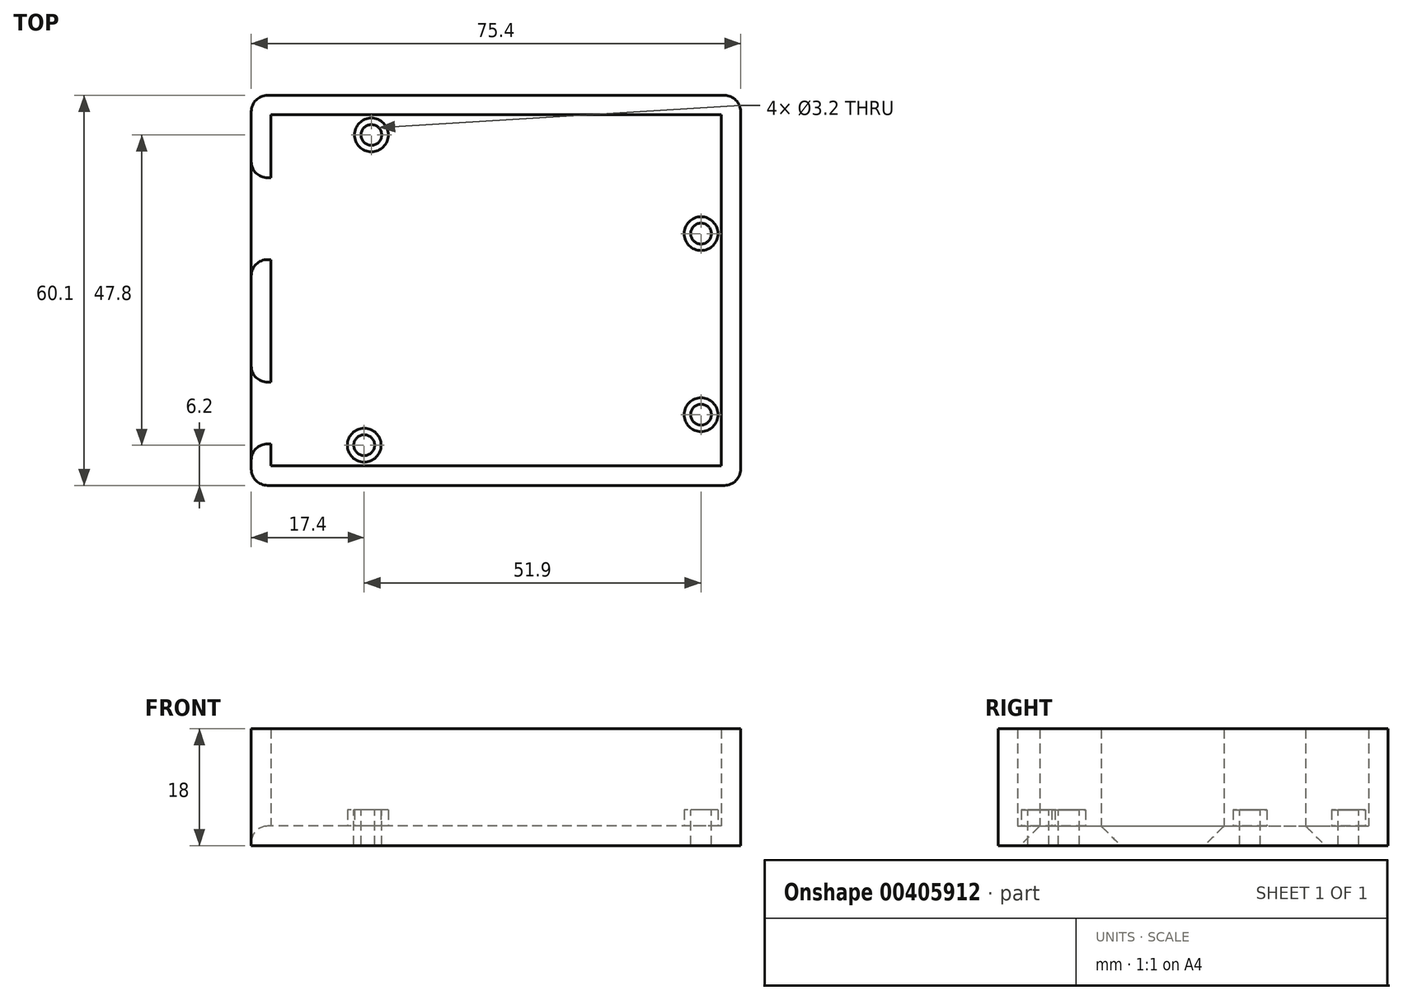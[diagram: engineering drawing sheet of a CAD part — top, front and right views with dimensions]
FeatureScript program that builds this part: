
annotation { "Feature Type Name" : "Feature", "Feature Type Description" : "" }
export const myFeature = defineFeature(function(context is Context, id is Id, definition is map)
    precondition{}
    {
        {
            var Q0;
            Q0=qCreatedBy(makeId("Top.planeOp"),FACE);
            var sketch = newSketch(context, id + "F0", { "sketchPlane" : qUnion([Q0])});
            skLineSegment(sketch, "E0.bottom", {"start": v(34.3, -26.65) * mm, "end": v(-34.3, -26.65) * mm});
            skLineSegment(sketch, "E0.top", {"start": v(34.3, 26.65) * mm, "end": v(-34.3, 26.65) * mm});
            skLineSegment(sketch, "E0.left", {"start": v(34.3, -26.65) * mm, "end": v(34.3, 26.65) * mm});
            skLineSegment(sketch, "E0.right", {"start": v(-34.3, -26.65) * mm, "end": v(-34.3, 26.65) * mm});
            skPoint(sketch, "E0.middle", {"position": v(0, 0) * mm});
            skCircle(sketch, "E1", {"center": v(-19.2, 23.95) * mm, "radius": 1.6 * mm});
            skCircle(sketch, "E2", {"center": v(31.6, 8.75) * mm, "radius": 1.6 * mm});
            skCircle(sketch, "E3", {"center": v(31.6, -19.15) * mm, "radius": 1.6 * mm});
            skCircle(sketch, "E4", {"center": v(-20.3, -23.85) * mm, "radius": 1.6 * mm});
            skLineSegment(sketch, "E5.0", {"start": v(34.7, 27.05) * mm, "end": v(-34.7, 27.05) * mm});
            skLineSegment(sketch, "E5.1", {"start": v(34.7, -27.05) * mm, "end": v(34.7, 27.05) * mm});
            skLineSegment(sketch, "E5.2", {"start": v(34.7, -27.05) * mm, "end": v(-34.7, -27.05) * mm});
            skLineSegment(sketch, "E5.3", {"start": v(-34.7, -27.05) * mm, "end": v(-34.7, 27.05) * mm});
            skLineSegment(sketch, "E6.0", {"start": v(37.7, 30.05) * mm, "end": v(-37.7, 30.05) * mm});
            skLineSegment(sketch, "E6.1", {"start": v(37.7, -30.05) * mm, "end": v(37.7, 30.05) * mm});
            skLineSegment(sketch, "E6.2", {"start": v(37.7, -30.05) * mm, "end": v(-37.7, -30.05) * mm});
            skLineSegment(sketch, "E6.3", {"start": v(-37.7, -30.05) * mm, "end": v(-37.7, 30.05) * mm});
            skLineSegment(sketch, "E7.bottom", {"start": v(-24, 5.05) * mm, "end": v(-40.5, 5.05) * mm});
            skLineSegment(sketch, "E7.top", {"start": v(-24, 17.05) * mm, "end": v(-40.5, 17.05) * mm});
            skLineSegment(sketch, "E7.left", {"start": v(-24, 5.05) * mm, "end": v(-24, 17.05) * mm});
            skLineSegment(sketch, "E7.right", {"start": v(-40.5, 5.05) * mm, "end": v(-40.5, 17.05) * mm});
            skPoint(sketch, "E7.middle", {"position": v(-32.25, 11.05) * mm});
            skLineSegment(sketch, "E8.bottom", {"start": v(-24.8, -23.35) * mm, "end": v(-39.3, -23.35) * mm});
            skLineSegment(sketch, "E8.top", {"start": v(-24.8, -14.45) * mm, "end": v(-39.3, -14.45) * mm});
            skLineSegment(sketch, "E8.left", {"start": v(-24.8, -23.35) * mm, "end": v(-24.8, -14.45) * mm});
            skLineSegment(sketch, "E8.right", {"start": v(-39.3, -23.35) * mm, "end": v(-39.3, -14.45) * mm});
            skPoint(sketch, "E8.middle", {"position": v(-32.05, -18.9) * mm});
            skCircle(sketch, "E9.0", {"center": v(-19.2, 23.95) * mm, "radius": 2.6 * mm});
            skCircle(sketch, "E10.0", {"center": v(-20.3, -23.85) * mm, "radius": 2.6 * mm});
            skCircle(sketch, "E11.0", {"center": v(31.6, -19.15) * mm, "radius": 2.6 * mm});
            skCircle(sketch, "E12.0", {"center": v(31.6, 8.75) * mm, "radius": 2.6 * mm});
            skLineSegment(sketch, "E13.0", {"start": v(-23.7, 4.75) * mm, "end": v(-40.8, 4.75) * mm});
            skLineSegment(sketch, "E13.1", {"start": v(-23.7, 4.75) * mm, "end": v(-23.7, 17.35) * mm});
            skLineSegment(sketch, "E13.2", {"start": v(-23.7, 17.35) * mm, "end": v(-40.8, 17.35) * mm});
            skLineSegment(sketch, "E13.3", {"start": v(-40.8, 4.75) * mm, "end": v(-40.8, 17.35) * mm});
            skLineSegment(sketch, "E14.0", {"start": v(-24.5, -14.15) * mm, "end": v(-39.6, -14.15) * mm});
            skLineSegment(sketch, "E14.1", {"start": v(-24.5, -23.65) * mm, "end": v(-24.5, -14.15) * mm});
            skLineSegment(sketch, "E14.2", {"start": v(-24.5, -23.65) * mm, "end": v(-39.6, -23.65) * mm});
            skLineSegment(sketch, "E14.3", {"start": v(-39.6, -23.65) * mm, "end": v(-39.6, -14.15) * mm});
            skSolve(sketch);
        }
        {
            var Q0;
            {var subQ4=sQuery(id+"F0.wireOp",EDGE,"E5.0");Q0=makeQuery(id+"F0.imprint","IMPRINT",FACE,{"disambiguationData":[TD([[makeQuery(id+"F0.imprint","IMPRINT",EDGE,{"derivedFrom":subQ4}),-1.0]])]});}
            var Q1;
            {var subQ0=sQuery(id+"F0.wireOp",EDGE,"E8.top");var subQ1=sQuery(id+"F0.wireOp",EDGE,"E0.right");var subQ2=makeQuery(id+"F0.imprint","INTERSECT",VERTEX,{"derivedFrom":[subQ1,subQ0]});Q1=makeQuery(id+"F0.imprint","IMPRINT",FACE,{"disambiguationData":[TD([[makeQuery(id+"F0.imprint","IMPRINT",EDGE,{"disambiguationData":[TD([[subQ2,-1.0]])],"derivedFrom":subQ1}),1.0]])]});}
            var Q2;
            {var subQ0=sQuery(id+"F0.wireOp",EDGE,"E8.bottom");var subQ1=sQuery(id+"F0.wireOp",EDGE,"E0.right");var subQ2=makeQuery(id+"F0.imprint","INTERSECT",VERTEX,{"derivedFrom":[subQ1,subQ0]});Q2=makeQuery(id+"F0.imprint","IMPRINT",FACE,{"disambiguationData":[TD([[makeQuery(id+"F0.imprint","IMPRINT",EDGE,{"disambiguationData":[TD([[subQ2,-1.0]])],"derivedFrom":subQ1}),1.0]])]});}
            var Q3;
            {var subQ0=sQuery(id+"F0.wireOp",EDGE,"E8.bottom");var subQ1=sQuery(id+"F0.wireOp",EDGE,"E0.right");var subQ2=makeQuery(id+"F0.imprint","INTERSECT",VERTEX,{"derivedFrom":[subQ1,subQ0]});Q3=makeQuery(id+"F0.imprint","IMPRINT",FACE,{"disambiguationData":[TD([[makeQuery(id+"F0.imprint","IMPRINT",EDGE,{"disambiguationData":[TD([[subQ2,-1.0]])],"derivedFrom":subQ1}),-1.0]])]});}
            var Q4;
            {var subQ4=sQuery(id+"F0.wireOp",EDGE,"E0.bottom");Q4=makeQuery(id+"F0.imprint","IMPRINT",FACE,{"disambiguationData":[TD([[makeQuery(id+"F0.imprint","IMPRINT",EDGE,{"derivedFrom":subQ4}),-1.0]])]});}
            var Q5;
            {var subQ10=sQuery(id+"F0.wireOp",EDGE,"E0.bottom");Q5=makeQuery(id+"F0.imprint","IMPRINT",FACE,{"disambiguationData":[TD([[makeQuery(id+"F0.imprint","IMPRINT",EDGE,{"derivedFrom":subQ10}),1.0]])]});}
            var Q6;
            {var subQ5=sQuery(id+"F0.wireOp",EDGE,"E7.left");Q6=makeQuery(id+"F0.imprint","IMPRINT",FACE,{"disambiguationData":[TD([[makeQuery(id+"F0.imprint","IMPRINT",EDGE,{"derivedFrom":subQ5}),1.0]])]});}
            var Q7;
            {var subQ0=sQuery(id+"F0.wireOp",EDGE,"E7.bottom");var subQ1=sQuery(id+"F0.wireOp",EDGE,"E5.3");var subQ2=makeQuery(id+"F0.imprint","INTERSECT",VERTEX,{"derivedFrom":[subQ1,subQ0]});Q7=makeQuery(id+"F0.imprint","IMPRINT",FACE,{"disambiguationData":[TD([[makeQuery(id+"F0.imprint","IMPRINT",EDGE,{"disambiguationData":[TD([[subQ2,-1.0]])],"derivedFrom":subQ1}),1.0]])]});}
            var Q8;
            {var subQ0=sQuery(id+"F0.wireOp",EDGE,"E7.bottom");var subQ1=sQuery(id+"F0.wireOp",EDGE,"E0.right");var subQ2=makeQuery(id+"F0.imprint","INTERSECT",VERTEX,{"derivedFrom":[subQ1,subQ0]});Q8=makeQuery(id+"F0.imprint","IMPRINT",FACE,{"disambiguationData":[TD([[makeQuery(id+"F0.imprint","IMPRINT",EDGE,{"disambiguationData":[TD([[subQ2,-1.0]])],"derivedFrom":subQ1}),1.0]])]});}
            var Q9;
            {var subQ0=sQuery(id+"F0.wireOp",EDGE,"E8.bottom");var subQ1=sQuery(id+"F0.wireOp",EDGE,"E5.3");var subQ2=makeQuery(id+"F0.imprint","INTERSECT",VERTEX,{"derivedFrom":[subQ1,subQ0]});Q9=makeQuery(id+"F0.imprint","IMPRINT",FACE,{"disambiguationData":[TD([[makeQuery(id+"F0.imprint","IMPRINT",EDGE,{"disambiguationData":[TD([[subQ2,-1.0]])],"derivedFrom":subQ1}),1.0]])]});}
            var Q10;
            {var subQ0=sQuery(id+"F0.wireOp",EDGE,"E8.top");var subQ1=sQuery(id+"F0.wireOp",EDGE,"E5.3");var subQ2=makeQuery(id+"F0.imprint","INTERSECT",VERTEX,{"derivedFrom":[subQ1,subQ0]});Q10=makeQuery(id+"F0.imprint","IMPRINT",FACE,{"disambiguationData":[TD([[makeQuery(id+"F0.imprint","IMPRINT",EDGE,{"disambiguationData":[TD([[subQ2,-1.0]])],"derivedFrom":subQ1}),1.0]])]});}
            var Q11;
            Q11=makeQuery(id+"F0.imprint","IMPRINT",FACE,{"disambiguationData":[TD([[makeQuery(id+"F0.imprint","IMPRINT",EDGE,{"derivedFrom":sQuery(id+"F0.wireOp",EDGE,"E1")}),-1.0]])]});
            var Q12;
            Q12=makeQuery(id+"F0.imprint","IMPRINT",FACE,{"disambiguationData":[TD([[makeQuery(id+"F0.imprint","IMPRINT",EDGE,{"derivedFrom":sQuery(id+"F0.wireOp",EDGE,"E4")}),-1.0]])]});
            var Q13;
            Q13=makeQuery(id+"F0.imprint","IMPRINT",FACE,{"disambiguationData":[TD([[makeQuery(id+"F0.imprint","IMPRINT",EDGE,{"derivedFrom":sQuery(id+"F0.wireOp",EDGE,"E3")}),-1.0]])]});
            var Q14;
            Q14=makeQuery(id+"F0.imprint","IMPRINT",FACE,{"disambiguationData":[TD([[makeQuery(id+"F0.imprint","IMPRINT",EDGE,{"derivedFrom":sQuery(id+"F0.wireOp",EDGE,"E2")}),-1.0]])]});
            var Q15;
            {var subQ0=sQuery(id+"F0.wireOp",EDGE,"E13.0");var subQ1=sQuery(id+"F0.wireOp",EDGE,"E5.3");var subQ2=makeQuery(id+"F0.imprint","INTERSECT",VERTEX,{"derivedFrom":[subQ1,subQ0]});Q15=makeQuery(id+"F0.imprint","IMPRINT",FACE,{"disambiguationData":[TD([[makeQuery(id+"F0.imprint","IMPRINT",EDGE,{"disambiguationData":[TD([[subQ2,-1.0]])],"derivedFrom":subQ1}),1.0]])]});}
            var Q16;
            {var subQ0=sQuery(id+"F0.wireOp",EDGE,"E13.0");var subQ1=sQuery(id+"F0.wireOp",EDGE,"E0.right");var subQ2=makeQuery(id+"F0.imprint","INTERSECT",VERTEX,{"derivedFrom":[subQ1,subQ0]});Q16=makeQuery(id+"F0.imprint","IMPRINT",FACE,{"disambiguationData":[TD([[makeQuery(id+"F0.imprint","IMPRINT",EDGE,{"disambiguationData":[TD([[subQ2,-1.0]])],"derivedFrom":subQ1}),1.0]])]});}
            var Q17;
            {var subQ0=sQuery(id+"F0.wireOp",EDGE,"E7.left");Q17=makeQuery(id+"F0.imprint","IMPRINT",FACE,{"disambiguationData":[TD([[makeQuery(id+"F0.imprint","IMPRINT",EDGE,{"derivedFrom":subQ0}),-1.0]])]});}
            var Q18;
            {var subQ0=sQuery(id+"F0.wireOp",EDGE,"E14.0");var subQ1=sQuery(id+"F0.wireOp",EDGE,"E0.right");var subQ2=makeQuery(id+"F0.imprint","INTERSECT",VERTEX,{"derivedFrom":[subQ1,subQ0]});Q18=makeQuery(id+"F0.imprint","IMPRINT",FACE,{"disambiguationData":[TD([[makeQuery(id+"F0.imprint","IMPRINT",EDGE,{"disambiguationData":[TD([[subQ2,-1.0]])],"derivedFrom":subQ1}),1.0]])]});}
            var Q19;
            {var subQ0=sQuery(id+"F0.wireOp",EDGE,"E14.0");var subQ1=sQuery(id+"F0.wireOp",EDGE,"E5.3");var subQ2=makeQuery(id+"F0.imprint","INTERSECT",VERTEX,{"derivedFrom":[subQ1,subQ0]});Q19=makeQuery(id+"F0.imprint","IMPRINT",FACE,{"disambiguationData":[TD([[makeQuery(id+"F0.imprint","IMPRINT",EDGE,{"disambiguationData":[TD([[subQ2,-1.0]])],"derivedFrom":subQ1}),1.0]])]});}
            var Q20;
            {var subQ0=sQuery(id+"F0.wireOp",EDGE,"E8.left");Q20=makeQuery(id+"F0.imprint","IMPRINT",FACE,{"disambiguationData":[TD([[makeQuery(id+"F0.imprint","IMPRINT",EDGE,{"derivedFrom":subQ0}),-1.0]])]});}
            var Q21;
            {var subQ0=sQuery(id+"F0.wireOp",EDGE,"E7.top");var subQ1=sQuery(id+"F0.wireOp",EDGE,"E5.3");var subQ2=makeQuery(id+"F0.imprint","INTERSECT",VERTEX,{"derivedFrom":[subQ1,subQ0]});Q21=makeQuery(id+"F0.imprint","IMPRINT",FACE,{"disambiguationData":[TD([[makeQuery(id+"F0.imprint","IMPRINT",EDGE,{"disambiguationData":[TD([[subQ2,-1.0]])],"derivedFrom":subQ1}),1.0]])]});}
            var Q22;
            {var subQ0=sQuery(id+"F0.wireOp",EDGE,"E7.top");var subQ1=sQuery(id+"F0.wireOp",EDGE,"E0.right");var subQ2=makeQuery(id+"F0.imprint","INTERSECT",VERTEX,{"derivedFrom":[subQ1,subQ0]});Q22=makeQuery(id+"F0.imprint","IMPRINT",FACE,{"disambiguationData":[TD([[makeQuery(id+"F0.imprint","IMPRINT",EDGE,{"disambiguationData":[TD([[subQ2,-1.0]])],"derivedFrom":subQ1}),1.0]])]});}
            var Q23;
            {var subQ0=sQuery(id+"F0.wireOp",EDGE,"E14.2");var subQ1=sQuery(id+"F0.wireOp",EDGE,"E0.right");var subQ2=makeQuery(id+"F0.imprint","INTERSECT",VERTEX,{"derivedFrom":[subQ1,subQ0]});Q23=makeQuery(id+"F0.imprint","IMPRINT",FACE,{"disambiguationData":[TD([[makeQuery(id+"F0.imprint","IMPRINT",EDGE,{"disambiguationData":[TD([[subQ2,-1.0]])],"derivedFrom":subQ1}),1.0]])]});}
            var Q24;
            {var subQ0=sQuery(id+"F0.wireOp",EDGE,"E14.2");var subQ1=sQuery(id+"F0.wireOp",EDGE,"E5.3");var subQ2=makeQuery(id+"F0.imprint","INTERSECT",VERTEX,{"derivedFrom":[subQ1,subQ0]});Q24=makeQuery(id+"F0.imprint","IMPRINT",FACE,{"disambiguationData":[TD([[makeQuery(id+"F0.imprint","IMPRINT",EDGE,{"disambiguationData":[TD([[subQ2,-1.0]])],"derivedFrom":subQ1}),1.0]])]});}
            extrude(context, id + "F1", {"entities" : qUnion([Q0, Q1, Q2, Q3, Q4, Q5, Q6, Q7, Q8, Q9, Q10, Q11, Q12, Q13, Q14, Q15, Q16, Q17, Q18, Q19, Q20, Q21, Q22, Q23, Q24]), "oppositeDirection" : true, "depth" : 3 * mm});
        }
        {
            var Q0;
            {var subQ11=sQuery(id+"F0.wireOp",EDGE,"E5.0");Q0=makeQuery(id+"F0.imprint","IMPRINT",FACE,{"disambiguationData":[TD([[makeQuery(id+"F0.imprint","IMPRINT",EDGE,{"derivedFrom":subQ11}),-1.0]])]});}
            var Q1;
            {var subQ0=sQuery(id+"F0.wireOp",EDGE,"E14.0");var subQ1=sQuery(id+"F0.wireOp",EDGE,"E5.3");var subQ2=makeQuery(id+"F0.imprint","INTERSECT",VERTEX,{"derivedFrom":[subQ1,subQ0]});Q1=makeQuery(id+"F0.imprint","IMPRINT",FACE,{"disambiguationData":[TD([[makeQuery(id+"F0.imprint","IMPRINT",EDGE,{"disambiguationData":[TD([[subQ2,-1.0]])],"derivedFrom":subQ1}),1.0]])]});}
            extrude(context, id + "F2", {"entities" : qUnion([Q0, Q1]), "operationType" : NewBodyOperationType.ADD, "depth" : 15 * mm});
        }
        {
            var Q0;
            Q0=makeQuery(id+"F0.imprint","IMPRINT",FACE,{"disambiguationData":[TD([[makeQuery(id+"F0.imprint","IMPRINT",EDGE,{"derivedFrom":sQuery(id+"F0.wireOp",EDGE,"E4")}),-1.0]])]});
            var Q1;
            Q1=makeQuery(id+"F0.imprint","IMPRINT",FACE,{"disambiguationData":[TD([[makeQuery(id+"F0.imprint","IMPRINT",EDGE,{"derivedFrom":sQuery(id+"F0.wireOp",EDGE,"E1")}),-1.0]])]});
            var Q2;
            Q2=makeQuery(id+"F0.imprint","IMPRINT",FACE,{"disambiguationData":[TD([[makeQuery(id+"F0.imprint","IMPRINT",EDGE,{"derivedFrom":sQuery(id+"F0.wireOp",EDGE,"E2")}),-1.0]])]});
            var Q3;
            Q3=makeQuery(id+"F0.imprint","IMPRINT",FACE,{"disambiguationData":[TD([[makeQuery(id+"F0.imprint","IMPRINT",EDGE,{"derivedFrom":sQuery(id+"F0.wireOp",EDGE,"E3")}),-1.0]])]});
            extrude(context, id + "F3", {"entities" : qUnion([Q0, Q1, Q2, Q3]), "operationType" : NewBodyOperationType.ADD, "depth" : 2.5 * mm});
        }
        {
            var Q0;
            {var subQ0=sQuery(id+"F0.wireOp",EDGE,"E6.2");var subQ1=sQuery(id+"F0.wireOp",EDGE,"E6.1");Q0=makeQuery(id+"F2.boolean.opBoolean","MERGE",EDGE,{"derivedFrom":[makeQuery(id+"F1.opExtrude","SWEPT_EDGE",EDGE,{"disambiguationData":[OSD([subQ1,subQ0])]}),makeQuery(id+"F2.opExtrude","SWEPT_EDGE",EDGE,{"disambiguationData":[OSD([subQ1,subQ0])]})]});}
            var Q1;
            {var subQ0=sQuery(id+"F0.wireOp",EDGE,"E6.1");var subQ1=sQuery(id+"F0.wireOp",EDGE,"E6.0");Q1=makeQuery(id+"F2.boolean.opBoolean","MERGE",EDGE,{"derivedFrom":[makeQuery(id+"F1.opExtrude","SWEPT_EDGE",EDGE,{"disambiguationData":[OSD([subQ1,subQ0])]}),makeQuery(id+"F2.opExtrude","SWEPT_EDGE",EDGE,{"disambiguationData":[OSD([subQ1,subQ0])]})]});}
            var Q2;
            {var subQ0=sQuery(id+"F0.wireOp",EDGE,"E6.3");var subQ1=sQuery(id+"F0.wireOp",EDGE,"E6.0");Q2=makeQuery(id+"F2.boolean.opBoolean","MERGE",EDGE,{"derivedFrom":[makeQuery(id+"F1.opExtrude","SWEPT_EDGE",EDGE,{"disambiguationData":[OSD([subQ1,subQ0])]}),makeQuery(id+"F2.opExtrude","SWEPT_EDGE",EDGE,{"disambiguationData":[OSD([subQ1,subQ0])]})]});}
            var Q3;
            {var subQ0=sQuery(id+"F0.wireOp",EDGE,"E6.3");var subQ1=sQuery(id+"F0.wireOp",EDGE,"E6.2");Q3=makeQuery(id+"F2.boolean.opBoolean","MERGE",EDGE,{"derivedFrom":[makeQuery(id+"F1.opExtrude","SWEPT_EDGE",EDGE,{"disambiguationData":[OSD([subQ1,subQ0])]}),makeQuery(id+"F2.opExtrude","SWEPT_EDGE",EDGE,{"disambiguationData":[OSD([subQ1,subQ0])]})]});}
            var Q4;
            Q4=makeQuery(id+"F2.opExtrude","SWEPT_EDGE",EDGE,{"disambiguationData":[OSD([sQuery(id+"F0.wireOp",EDGE,"E6.3"),sQuery(id+"F0.wireOp",EDGE,"E14.0")])]});
            var Q5;
            Q5=makeQuery(id+"F2.opExtrude","SWEPT_EDGE",EDGE,{"disambiguationData":[OSD([sQuery(id+"F0.wireOp",EDGE,"E6.3"),sQuery(id+"F0.wireOp",EDGE,"E13.2")])]});
            var Q6;
            Q6=makeQuery(id+"F2.opExtrude","SWEPT_EDGE",EDGE,{"disambiguationData":[OSD([sQuery(id+"F0.wireOp",EDGE,"E6.3"),sQuery(id+"F0.wireOp",EDGE,"E13.0")])]});
            var Q7;
            Q7=makeQuery(id+"F2.opExtrude","SWEPT_EDGE",EDGE,{"disambiguationData":[OSD([sQuery(id+"F0.wireOp",EDGE,"E6.3"),sQuery(id+"F0.wireOp",EDGE,"E14.2")])]});
            var Q8;
            {var subQ0=sQuery(id+"F0.wireOp",EDGE,"E5.3");Q8=makeQuery(id+"F2.opExtrude","CAP_EDGE",EDGE,{"disambiguationData":[OSD([subQ0]),TDD([makeQuery(id+"F0.imprint","IMPRINT",EDGE,{"disambiguationData":[TD([[makeQuery(id+"F0.imprint","INTERSECT",VERTEX,{"derivedFrom":[sQuery(id+"F0.wireOp",EDGE,"E5.0"),subQ0]}),1.0]])],"derivedFrom":subQ0})])],"isStart":true});}
            var Q9;
            Q9=makeQuery(id+"F2.opExtrude","CAP_EDGE",EDGE,{"disambiguationData":[OSD([sQuery(id+"F0.wireOp",EDGE,"E5.0")])],"isStart":true});
            var Q10;
            {var subQ0=sQuery(id+"F0.wireOp",EDGE,"E5.3");Q10=makeQuery(id+"F2.opExtrude","CAP_EDGE",EDGE,{"disambiguationData":[OSD([subQ0]),TDD([makeQuery(id+"F0.imprint","IMPRINT",EDGE,{"disambiguationData":[TD([[makeQuery(id+"F0.imprint","INTERSECT",VERTEX,{"derivedFrom":[subQ0,sQuery(id+"F0.wireOp",EDGE,"E14.0")]}),-1.0]])],"derivedFrom":subQ0})])],"isStart":true});}
            var Q11;
            {var subQ0=sQuery(id+"F0.wireOp",EDGE,"E5.3");Q11=makeQuery(id+"F2.opExtrude","CAP_EDGE",EDGE,{"disambiguationData":[OSD([subQ0]),TDD([makeQuery(id+"F0.imprint","IMPRINT",EDGE,{"disambiguationData":[TD([[makeQuery(id+"F0.imprint","INTERSECT",VERTEX,{"derivedFrom":[sQuery(id+"F0.wireOp",EDGE,"E5.2"),subQ0]}),-1.0]])],"derivedFrom":subQ0})])],"isStart":true});}
            var Q12;
            Q12=makeQuery(id+"F2.opExtrude","CAP_EDGE",EDGE,{"disambiguationData":[OSD([sQuery(id+"F0.wireOp",EDGE,"E5.2")])],"isStart":true});
            var Q13;
            Q13=makeQuery(id+"F2.opExtrude","CAP_EDGE",EDGE,{"disambiguationData":[OSD([sQuery(id+"F0.wireOp",EDGE,"E5.1")])],"isStart":true});
            var Q14;
            Q14=makeQuery(id+"F3.opExtrude","CAP_EDGE",EDGE,{"disambiguationData":[OSD([sQuery(id+"F0.wireOp",EDGE,"E12.0")])],"isStart":true});
            var Q15;
            Q15=makeQuery(id+"F3.opExtrude","CAP_EDGE",EDGE,{"disambiguationData":[OSD([sQuery(id+"F0.wireOp",EDGE,"E11.0")])],"isStart":true});
            var Q16;
            Q16=makeQuery(id+"F3.opExtrude","CAP_EDGE",EDGE,{"disambiguationData":[OSD([sQuery(id+"F0.wireOp",EDGE,"E10.0")])],"isStart":true});
            var Q17;
            Q17=makeQuery(id+"F3.opExtrude","CAP_EDGE",EDGE,{"disambiguationData":[OSD([sQuery(id+"F0.wireOp",EDGE,"E9.0")])],"isStart":true});
            var Q18;
            {var subQ0=sQuery(id+"F0.wireOp",EDGE,"E6.3");var subQ2=sQuery(id+"F0.wireOp",EDGE,"E13.0");Q18=makeQuery(id+"F2.boolean.opBoolean","SPLIT",EDGE,{"disambiguationData":[TD([makeQuery(id+"F2.opExtrude","SWEPT_FACE",FACE,{"disambiguationData":[OSD([subQ2])]})])],"derivedFrom":makeQuery(id+"F1.opExtrude","CAP_EDGE",EDGE,{"disambiguationData":[OSD([subQ0])],"isStart":true})});}
            var Q19;
            {var subQ0=sQuery(id+"F0.wireOp",EDGE,"E6.3");var subQ3=sQuery(id+"F0.wireOp",EDGE,"E14.0");Q19=makeQuery(id+"F2.boolean.opBoolean","SPLIT",EDGE,{"disambiguationData":[TD([makeQuery(id+"F2.opExtrude","SWEPT_FACE",FACE,{"disambiguationData":[OSD([subQ3])]})])],"derivedFrom":makeQuery(id+"F1.opExtrude","CAP_EDGE",EDGE,{"disambiguationData":[OSD([subQ0])],"isStart":true})});}
            fillet(context, id + "F4", {"entities" : qUnion([Q0, Q1, Q2, Q3, Q4, Q5, Q6, Q7, Q8, Q9, Q10, Q11, Q12, Q13, Q14, Q15, Q16, Q17, Q18, Q19]), "radius" : 2.5 * mm, "tangentPropagation" : true, "allowEdgeOverflow" : false});
        }
    });
